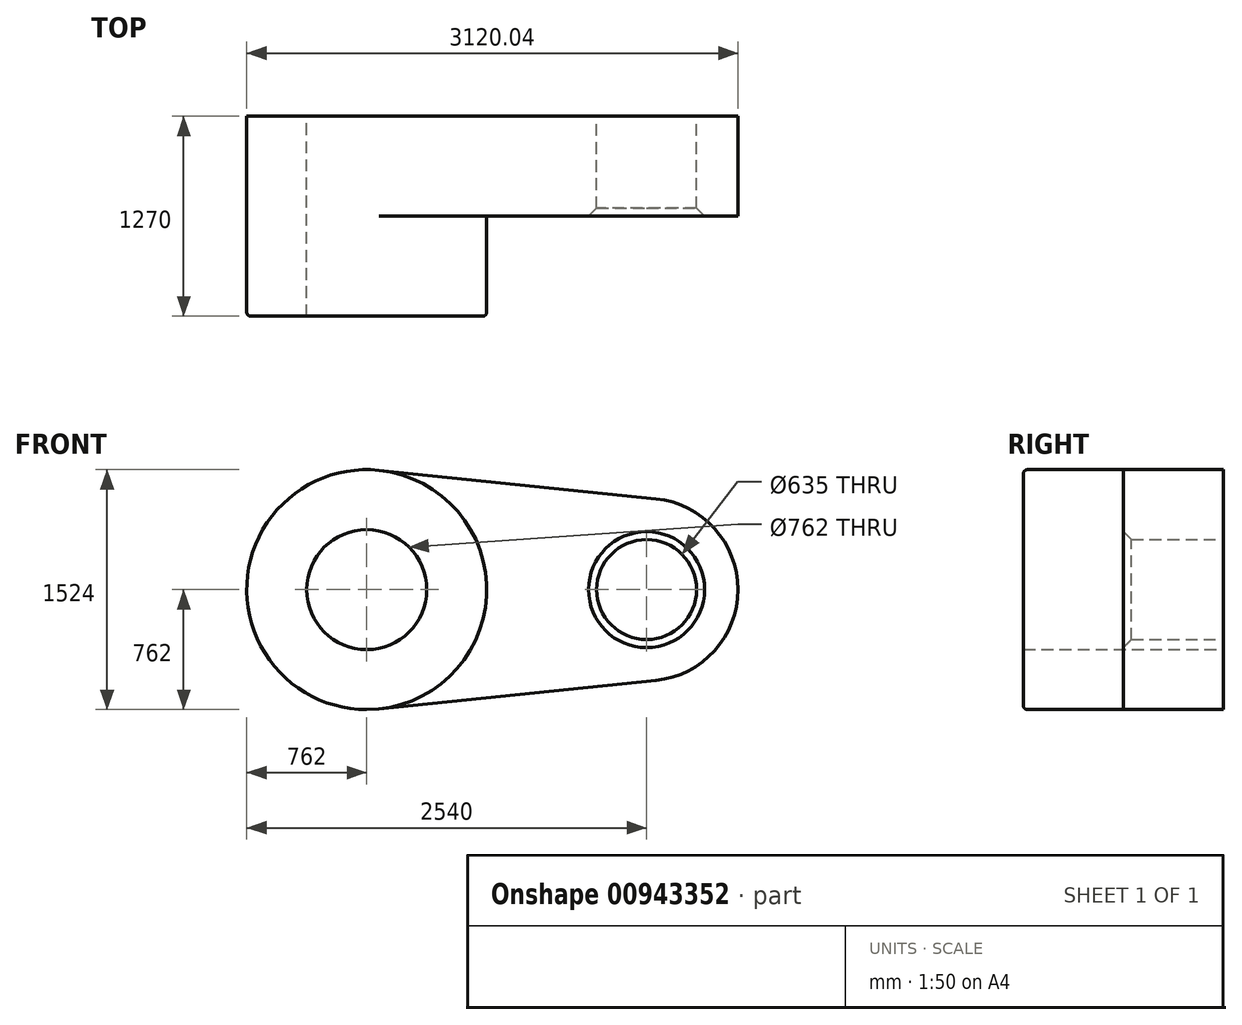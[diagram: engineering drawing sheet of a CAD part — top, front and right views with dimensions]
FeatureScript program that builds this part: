
annotation { "Feature Type Name" : "Feature", "Feature Type Description" : "" }
export const myFeature = defineFeature(function(context is Context, id is Id, definition is map)
    precondition{}
    {
        {
            var Q0;
            Q0=qCreatedBy(makeId("Front.planeOp"),FACE);
            var sketch = newSketch(context, id + "F0", { "sketchPlane" : qUnion([Q0])});
            skCircle(sketch, "E0", {"center": v(0, 0) * mm, "radius": 762 * mm});
            skCircle(sketch, "E1", {"center": v(1778, 0) * mm, "radius": 580.04 * mm});
            skLineSegment(sketch, "E2", {"start": v(77.98, 758) * mm, "end": v(1837.36, 577) * mm});
            skLineSegment(sketch, "E3", {"start": v(77.98, -758) * mm, "end": v(1837.36, -577) * mm});
            skCircle(sketch, "E4", {"center": v(0, 0) * mm, "radius": 381 * mm});
            skCircle(sketch, "E5", {"center": v(1778, 0) * mm, "radius": 317.5 * mm});
            skSolve(sketch);
        }
        {
            var Q0;
            Q0=makeQuery(id+"F0.imprint","IMPRINT",FACE,{"disambiguationData":[TD([[makeQuery(id+"F0.imprint","IMPRINT",EDGE,{"derivedFrom":sQuery(id+"F0.wireOp",EDGE,"E5")}),-1.0]])]});
            var Q1;
            Q1=makeQuery(id+"F0.imprint","IMPRINT",FACE,{"disambiguationData":[TD([[makeQuery(id+"F0.imprint","IMPRINT",EDGE,{"derivedFrom":sQuery(id+"F0.wireOp",EDGE,"E4")}),-1.0]])]});
            var Q2;
            {var subQ0=sQuery(id+"F0.wireOp",EDGE,"E2");Q2=makeQuery(id+"F0.imprint","IMPRINT",FACE,{"disambiguationData":[TD([[makeQuery(id+"F0.imprint","IMPRINT",EDGE,{"derivedFrom":subQ0}),-1.0]])]});}
            extrude(context, id + "F1", {"entities" : qUnion([Q0, Q1, Q2]), "depth" : 635 * mm, "offsetDistance" : 25.4 * mm});
        }
        {
            var Q0;
            Q0=makeQuery(id+"F0.imprint","IMPRINT",FACE,{"disambiguationData":[TD([[makeQuery(id+"F0.imprint","IMPRINT",EDGE,{"derivedFrom":sQuery(id+"F0.wireOp",EDGE,"E4")}),-1.0]])]});
            extrude(context, id + "F2", {"entities" : qUnion([Q0]), "operationType" : NewBodyOperationType.ADD, "depth" : 1270 * mm, "offsetDistance" : 25.4 * mm});
        }
        {
            var Q0;
            Q0=makeQuery(id+"F2.opExtrude","CAP_EDGE",EDGE,{"disambiguationData":[OSD([sQuery(id+"F0.wireOp",EDGE,"E0")])],"isStart":false});
            fillet(context, id + "F3", {"entities" : qUnion([Q0]), "radius" : 25.4 * mm, "tangentPropagation" : true, "allowEdgeOverflow" : false});
        }
        {
            var Q0;
            Q0=makeQuery(id+"F1.opExtrude","CAP_EDGE",EDGE,{"disambiguationData":[OSD([sQuery(id+"F0.wireOp",EDGE,"E5")])],"isStart":false});
            chamfer(context, id + "F4", {"entities" : qUnion([Q0]), "width" : 50.8 * mm, "tangentPropagation" : true});
        }
    });
